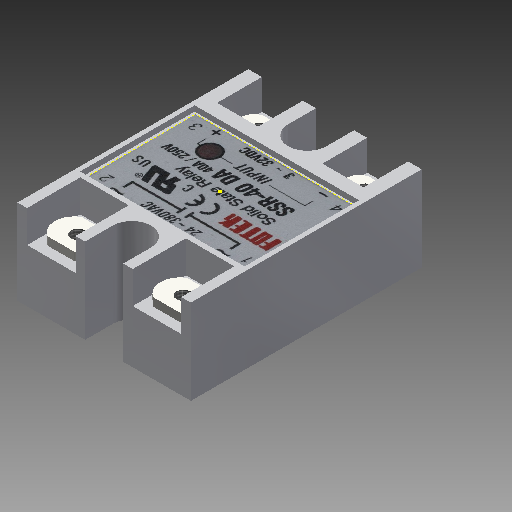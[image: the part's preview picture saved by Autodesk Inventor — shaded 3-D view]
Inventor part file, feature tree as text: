
AUTODESK INVENTOR PART (.ipt)
format: ipt  version: 2019 (Build 230136000, 136)  size: 480,256 bytes
history: native  units: in
note: dims shown in document units (in); Inventor stores cm internally (conversion verified against a paired STEP export)
features: sketch x11, extrude x9, thread x4, fillet x1, shell x1, other x1
ambient origin geometry x8: Origin, YZ Plane, XZ Plane, XY Plane, X Axis, Y Axis, Z Axis, Center Point
bodies: Solid1 (feature_tree)
feature tree (27):
  extrude  "Extrusion1"  Depth=2.355in
  extrude  "Extrusion2"  Depth=0.388in
  extrude  "Extrusion3"  Depth=0.194in
  extrude  "Extrusion4"  Depth=0.6905in
  extrude  "Extrusion5"  Depth=0.388in
  sketch  "Sketch6"  dims[d11=0.194in d12=0.194in]
  extrude  "Extrusion6"  Depth=0.194in
  extrude  "Extrusion7"  Depth=0.494in
  thread  "Thread1"  [1 undecoded]
  thread  "Thread2"  [1 undecoded]
  extrude  "Extrusion8"  Depth=0.542in
  extrude  "Extrusion9"  Depth=0.098in
  fillet  "Fillet1"  Radius=0.0985in
  thread  "Thread3"  [1 undecoded]
  thread  "Thread4"  [1 undecoded]
  shell  "Shell1"  Thickness=0.457in
  sketch  "Sketch11"  dims[d28=0.1335in d29=0.418in d30=0.457in d31=0.134in d32=0.1385in d33=0.308in d34=0.0in d35=1.677in d36=1.168in d37=0.056in d38=0.0in d39=0.344in d40=0.099in d41=0.099in d42=0.274in d43=0.11in d44=0.11in d45=0.11in d46=0.274in d47=0.11in d48=0.099in d49=0.099in d50=0.2in d51=0.2in d52=0.2in d53=0.2in d54=0.083in d55=0.0in d56=0.142in d57=0.271in d58=0.271in d59=0.247in d60=0.247in d61=0.271in d62=0.247in d63=0.275in d64=0.0in d65=1.0in d66=0.0in d67=1.0in d68=0.0in d69=0.259in d70=0.099in d71=0.099in d72=0.198in d73=0.11in d74=0.11in d75=0.1348in d76=0.0125in d77=0.1348in d78=0.0125in d79=0.11in d80=0.1348in d81=0.1348in d82=0.073in d83=0.0in d84=0.142in d85=0.142in d86=0.209in d87=0.209in d88=0.2285in d89=0.2285in d90=0.2285in d91=0.2285in d92=0.209in d93=0.209in d94=0.291in d95=0.0in d96=0.001in d97=1.0in d98=0.0in d99=1.0in d100=0.0in d101=0.1in]
  sketch  "Sketch1"  dims[d0=1.769in d1=2.355in]
  sketch  "Sketch2"  dims[d2=0.868in d3=0.0in d4=0.388in]
  sketch  "Sketch3"  dims[d5=0.478in d6=0.194in]
  sketch  "Sketch4"  dims[d7=0.6905in d8=0.6905in]
  sketch  "Sketch5"  dims[d9=0.388in d10=0.478in]
  sketch  "Sketch7"  dims[d13=0.868in d14=0.0in d15=0.494in d16=0.542in d17=0.099in]
  sketch  "Sketch8"  dims[d18=0.0975in d19=0.542in]
  sketch  "Sketch9"  dims[d20=0.494in d21=0.098in d22=0.0985in d23=0.327in d24=0.0in d25=0.418in d26=0.457in]
  sketch  "Sketch10"  dims[d27=0.139in]
  other  "Image1"
note: 4 required parameter values undecoded (feature->parameter linkage not recoverable at this tier; creation-order binding heuristic only, values carry confidence <= 0.55)
